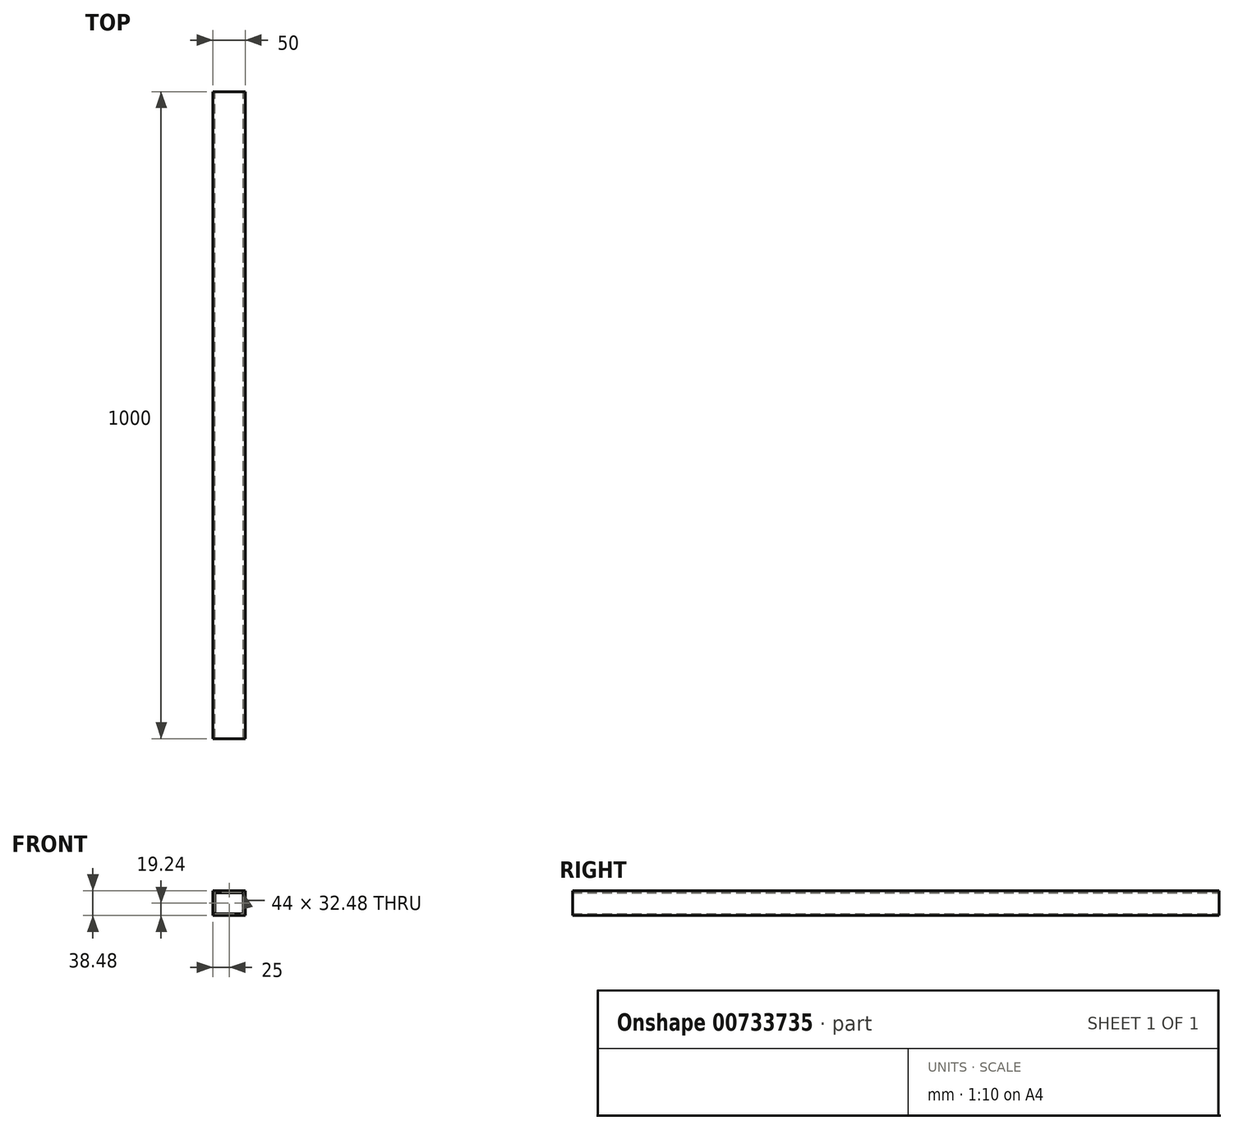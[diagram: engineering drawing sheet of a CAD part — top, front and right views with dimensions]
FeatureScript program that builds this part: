
annotation { "Feature Type Name" : "Feature", "Feature Type Description" : "" }
export const myFeature = defineFeature(function(context is Context, id is Id, definition is map)
    precondition{}
    {
        {
            var Q0;
            Q0=qCreatedBy(makeId("Front.planeOp"),FACE);
            var sketch = newSketch(context, id + "F0", { "sketchPlane" : qUnion([Q0])});
            skLineSegment(sketch, "E0.bottom", {"start": v(25, -19.24) * mm, "end": v(-25, -19.24) * mm});
            skLineSegment(sketch, "E0.top", {"start": v(25, 19.24) * mm, "end": v(-25, 19.24) * mm});
            skLineSegment(sketch, "E0.left", {"start": v(25, -19.24) * mm, "end": v(25, 19.24) * mm});
            skLineSegment(sketch, "E0.right", {"start": v(-25, -19.24) * mm, "end": v(-25, 19.24) * mm});
            skPoint(sketch, "E0.middle", {"position": v(0, 0) * mm});
            skLineSegment(sketch, "E1.0", {"start": v(22, 16.24) * mm, "end": v(-22, 16.24) * mm});
            skLineSegment(sketch, "E1.1", {"start": v(22, -16.24) * mm, "end": v(22, 16.24) * mm});
            skLineSegment(sketch, "E1.2", {"start": v(22, -16.24) * mm, "end": v(-22, -16.24) * mm});
            skLineSegment(sketch, "E1.3", {"start": v(-22, -16.24) * mm, "end": v(-22, 16.24) * mm});
            skSolve(sketch);
        }
        {
            var Q0;
            Q0=qSketchRegion(id+"F0",true);
            extrude(context, id + "F1", {"entities" : qUnion([Q0]), "depth" : 1000 * mm, "offsetDistance" : 25 * mm});
        }
    });
